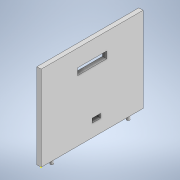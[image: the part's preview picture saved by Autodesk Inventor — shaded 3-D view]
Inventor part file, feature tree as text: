
AUTODESK INVENTOR PART (.ipt)
format: ipt  version: 2020 (Build 240168000, 168)  size: 133,120 bytes
history: native  units: mm
features: sketch x8, extrude x5
ambient origin geometry x8: Origin, YZ Plane, XZ Plane, XY Plane, X Axis, Y Axis, Z Axis, Center Point
bodies: Solid1 (feature_tree)
feature tree (13):
  extrude  "Extrusion1"  Depth=120.0mm
  extrude  "Extrusion2"  Depth=100.0mm
  extrude  "Extrusion3"  Depth=15.0mm
  sketch  "Sketch4"  dims[d7=5.0mm d8=0.0mm d9=2.5mm]
  sketch  "Sketch5"  dims[d10=15.0mm d11=3.5mm]
  sketch  "Sketch6"  dims[d12=5.0mm d13=0.0mm]
  extrude  "Extrusion4"  Depth=5.0mm
  extrude  "Extrusion5"  Depth=15.0mm
  sketch  "Sketch1"  dims[d0=5.0mm d1=120.0mm]
  sketch  "Sketch2"  dims[d2=100.0mm d3=0.0mm d4=2.5mm]
  sketch  "Sketch3"  dims[d5=15.0mm d6=3.5mm]
  sketch  "Sketch7"  dims[d14=42.838mm]
  sketch  "Sketch8"  dims[d15=20.0mm d16=34.336mm d17=8.0mm d18=10.0mm d19=0.0mm d20=60.0mm d21=15.0mm d22=10.0mm d23=5.0mm d24=10.0mm d25=0.0mm]
